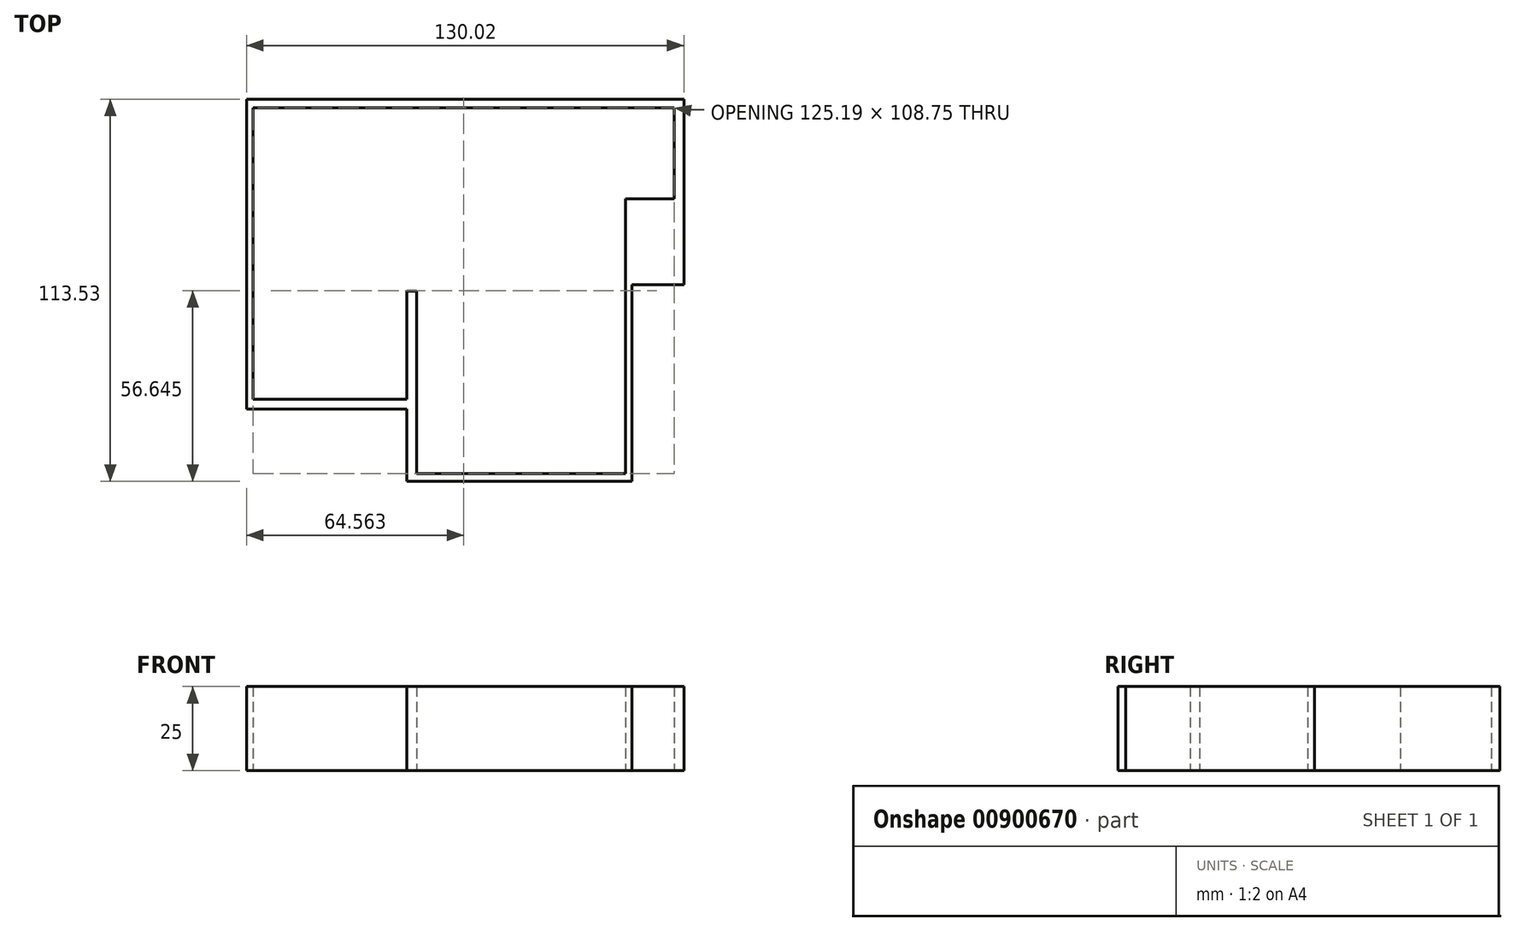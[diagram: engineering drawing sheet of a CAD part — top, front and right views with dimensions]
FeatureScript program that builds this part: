
annotation { "Feature Type Name" : "Feature", "Feature Type Description" : "" }
export const myFeature = defineFeature(function(context is Context, id is Id, definition is map)
    precondition{}
    {
        {
            var Q0;
            Q0=qCreatedBy(makeId("Top.planeOp"),FACE);
            var sketch = newSketch(context, id + "F0", { "sketchPlane" : qUnion([Q0])});
            skLineSegment(sketch, "E0.bottom", {"start": v(-59.3, 49.44) * mm, "end": v(-11.7, 49.44) * mm});
            skLineSegment(sketch, "E0.left", {"start": v(-59.3, 49.44) * mm, "end": v(-59.3, 21.38) * mm});
            skLineSegment(sketch, "E0.right", {"start": v(-11.7, 49.44) * mm, "end": v(-11.7, 21.38) * mm});
            skLineSegment(sketch, "E1.bottom", {"start": v(-11.7, 49.44) * mm, "end": v(39.76, 49.44) * mm});
            skLineSegment(sketch, "E1.left", {"start": v(-11.7, 21.38) * mm, "end": v(-11.7, 4.35) * mm});
            skLineSegment(sketch, "E1.right", {"start": v(39.76, 49.44) * mm, "end": v(39.76, 4.35) * mm});
            skLineSegment(sketch, "E2.top", {"start": v(-59.3, -42.66) * mm, "end": v(-11.7, -42.66) * mm});
            skLineSegment(sketch, "E2.left", {"start": v(-59.3, 21.38) * mm, "end": v(-59.3, -42.66) * mm});
            skLineSegment(sketch, "E2.right", {"start": v(-11.7, 21.38) * mm, "end": v(-11.7, -42.66) * mm});
            skLineSegment(sketch, "E3.top", {"start": v(-11.7, -61.82) * mm, "end": v(39.76, -61.82) * mm});
            skLineSegment(sketch, "E3.left", {"start": v(-11.7, 4.35) * mm, "end": v(-11.7, -61.82) * mm});
            skLineSegment(sketch, "E3.right", {"start": v(39.76, 4.35) * mm, "end": v(39.76, -23.9) * mm});
            skLineSegment(sketch, "E4.bottom", {"start": v(39.76, 49.44) * mm, "end": v(70.72, 49.44) * mm});
            skLineSegment(sketch, "E4.top", {"start": v(39.76, 19.83) * mm, "end": v(70.72, 19.83) * mm});
            skLineSegment(sketch, "E4.left", {"start": v(39.76, 49.44) * mm, "end": v(39.76, 19.83) * mm});
            skLineSegment(sketch, "E4.right", {"start": v(70.72, 49.44) * mm, "end": v(70.72, 19.83) * mm});
            skLineSegment(sketch, "E5.bottom", {"start": v(39.76, 19.83) * mm, "end": v(53.11, 19.83) * mm});
            skLineSegment(sketch, "E5.top", {"start": v(39.76, -23.9) * mm, "end": v(53.11, -23.9) * mm});
            skLineSegment(sketch, "E5.left", {"start": v(39.76, 19.83) * mm, "end": v(39.76, -23.9) * mm});
            skLineSegment(sketch, "E5.right", {"start": v(53.11, 19.83) * mm, "end": v(53.11, -23.9) * mm});
            skLineSegment(sketch, "E6.bottom", {"start": v(70.72, 19.83) * mm, "end": v(53.11, 19.83) * mm});
            skLineSegment(sketch, "E6.top", {"start": v(70.72, -5.7) * mm, "end": v(53.11, -5.7) * mm});
            skLineSegment(sketch, "E6.left", {"start": v(70.72, 19.83) * mm, "end": v(70.72, -5.7) * mm});
            skLineSegment(sketch, "E6.right", {"start": v(53.11, 19.83) * mm, "end": v(53.11, -5.7) * mm});
            skLineSegment(sketch, "E7.bottom", {"start": v(39.76, -23.9) * mm, "end": v(53.3, -23.9) * mm});
            skLineSegment(sketch, "E7.top", {"start": v(39.76, -61.82) * mm, "end": v(53.3, -61.82) * mm});
            skLineSegment(sketch, "E7.right", {"start": v(53.3, -23.9) * mm, "end": v(53.3, -61.82) * mm});
            skLineSegment(sketch, "E8", {"start": v(-11.7, -7.64) * mm, "end": v(39.76, -7.64) * mm});
            skLineSegment(sketch, "E9", {"start": v(-59.3, 8.9) * mm, "end": v(-11.7, 8.9) * mm});
            skLineSegment(sketch, "E10.bottom", {"start": v(-59.3, 8.9) * mm, "end": v(-57.33, 8.9) * mm});
            skLineSegment(sketch, "E10.top", {"start": v(-59.3, 49.44) * mm, "end": v(-57.33, 49.44) * mm});
            skLineSegment(sketch, "E10.left", {"start": v(-59.3, 8.9) * mm, "end": v(-59.3, 49.44) * mm});
            skLineSegment(sketch, "E10.right", {"start": v(-57.33, 8.9) * mm, "end": v(-57.33, 49.44) * mm});
            skLineSegment(sketch, "E11.bottom", {"start": v(-57.33, 49.44) * mm, "end": v(70.72, 49.44) * mm});
            skLineSegment(sketch, "E11.top", {"start": v(-57.33, 46.93) * mm, "end": v(70.72, 46.93) * mm});
            skLineSegment(sketch, "E11.left", {"start": v(-57.33, 49.44) * mm, "end": v(-57.33, 46.93) * mm});
            skLineSegment(sketch, "E11.right", {"start": v(70.72, 49.44) * mm, "end": v(70.72, 46.93) * mm});
            skLineSegment(sketch, "E12.bottom", {"start": v(70.72, 46.93) * mm, "end": v(67.86, 46.93) * mm});
            skLineSegment(sketch, "E12.top", {"start": v(70.72, -5.7) * mm, "end": v(67.86, -5.7) * mm});
            skLineSegment(sketch, "E12.left", {"start": v(70.72, 46.93) * mm, "end": v(70.72, -5.7) * mm});
            skLineSegment(sketch, "E12.right", {"start": v(67.86, 46.93) * mm, "end": v(67.86, -5.7) * mm});
            skLineSegment(sketch, "E13.bottom", {"start": v(-59.3, -42.66) * mm, "end": v(-57.33, -42.66) * mm});
            skLineSegment(sketch, "E13.left", {"start": v(-59.3, -42.66) * mm, "end": v(-59.3, 8.9) * mm});
            skLineSegment(sketch, "E13.right", {"start": v(-57.33, -42.66) * mm, "end": v(-57.33, 8.9) * mm});
            skLineSegment(sketch, "E14.bottom", {"start": v(-57.33, 8.9) * mm, "end": v(-11.7, 8.9) * mm});
            skLineSegment(sketch, "E14.top", {"start": v(-57.33, 6.68) * mm, "end": v(-11.7, 6.68) * mm});
            skLineSegment(sketch, "E14.left", {"start": v(-57.33, 8.9) * mm, "end": v(-57.33, 6.68) * mm});
            skLineSegment(sketch, "E14.right", {"start": v(-11.7, 8.9) * mm, "end": v(-11.7, 6.68) * mm});
            skLineSegment(sketch, "E15.bottom", {"start": v(-11.7, -61.82) * mm, "end": v(-8.77, -61.82) * mm});
            skLineSegment(sketch, "E15.top", {"start": v(-11.7, 46.93) * mm, "end": v(-8.77, 46.93) * mm});
            skLineSegment(sketch, "E15.left", {"start": v(-11.7, -61.82) * mm, "end": v(-11.7, 46.93) * mm});
            skLineSegment(sketch, "E15.right", {"start": v(-8.77, -61.82) * mm, "end": v(-8.77, 46.93) * mm});
            skLineSegment(sketch, "E16.bottom", {"start": v(-57.33, -42.66) * mm, "end": v(-11.7, -42.66) * mm});
            skLineSegment(sketch, "E16.top", {"start": v(-57.33, -39.75) * mm, "end": v(-11.7, -39.75) * mm});
            skLineSegment(sketch, "E16.left", {"start": v(-57.33, -42.66) * mm, "end": v(-57.33, -39.75) * mm});
            skLineSegment(sketch, "E16.right", {"start": v(-11.7, -42.66) * mm, "end": v(-11.7, -39.75) * mm});
            skLineSegment(sketch, "E17.bottom", {"start": v(39.76, -23.9) * mm, "end": v(37.1, -23.9) * mm});
            skLineSegment(sketch, "E17.top", {"start": v(39.76, 46.93) * mm, "end": v(37.1, 46.93) * mm});
            skLineSegment(sketch, "E17.left", {"start": v(39.76, -23.9) * mm, "end": v(39.76, 46.93) * mm});
            skLineSegment(sketch, "E17.right", {"start": v(37.1, -23.9) * mm, "end": v(37.1, 46.93) * mm});
            skLineSegment(sketch, "E18.bottom", {"start": v(39.76, 19.83) * mm, "end": v(67.86, 19.83) * mm});
            skLineSegment(sketch, "E18.top", {"start": v(39.76, 22.36) * mm, "end": v(67.86, 22.36) * mm});
            skLineSegment(sketch, "E18.left", {"start": v(39.76, 19.83) * mm, "end": v(39.76, 22.36) * mm});
            skLineSegment(sketch, "E18.right", {"start": v(67.86, 19.83) * mm, "end": v(67.86, 22.36) * mm});
            skLineSegment(sketch, "E19.bottom", {"start": v(53.3, -23.9) * mm, "end": v(39.76, -23.9) * mm});
            skLineSegment(sketch, "E19.top", {"start": v(53.3, -20.98) * mm, "end": v(39.76, -20.98) * mm});
            skLineSegment(sketch, "E19.left", {"start": v(53.3, -23.9) * mm, "end": v(53.3, -20.98) * mm});
            skLineSegment(sketch, "E19.right", {"start": v(39.76, -23.9) * mm, "end": v(39.76, -20.98) * mm});
            skLineSegment(sketch, "E20.bottom", {"start": v(53.3, -61.82) * mm, "end": v(55.24, -61.82) * mm});
            skLineSegment(sketch, "E20.top", {"start": v(53.3, 19.83) * mm, "end": v(55.24, 19.83) * mm});
            skLineSegment(sketch, "E20.left", {"start": v(53.3, -61.82) * mm, "end": v(53.3, 19.83) * mm});
            skLineSegment(sketch, "E20.right", {"start": v(55.24, -61.82) * mm, "end": v(55.24, 19.83) * mm});
            skLineSegment(sketch, "E21.bottom", {"start": v(-11.7, -61.82) * mm, "end": v(55.24, -61.82) * mm});
            skLineSegment(sketch, "E21.top", {"start": v(-11.7, -64.1) * mm, "end": v(55.24, -64.1) * mm});
            skLineSegment(sketch, "E21.left", {"start": v(-11.7, -61.82) * mm, "end": v(-11.7, -64.1) * mm});
            skLineSegment(sketch, "E21.right", {"start": v(55.24, -61.82) * mm, "end": v(55.24, -64.1) * mm});
            skSolve(sketch);
        }
        {
            var Q0;
            Q0 = qSketchRegion(id + "F0", true);
            extrude(context, id + "F1", {"entities" : qUnion([Q0]), "depth" : 25 * mm, "offsetDistance" : 25 * mm});
        }
        {
            var Q0;
            Q0 = qSketchRegion(id + "F0", true);
            extrude(context, id + "F2", {"entities" : qUnion([Q0]), "operationType" : NewBodyOperationType.ADD, "depth" : 25 * mm, "offsetDistance" : 25 * mm});
        }
        {
            var Q0;
            Q0 = qSketchRegion(id + "F0", true);
            extrude(context, id + "F3", {"entities" : qUnion([Q0]), "operationType" : NewBodyOperationType.ADD, "depth" : 25 * mm, "offsetDistance" : 25 * mm});
        }
    });
